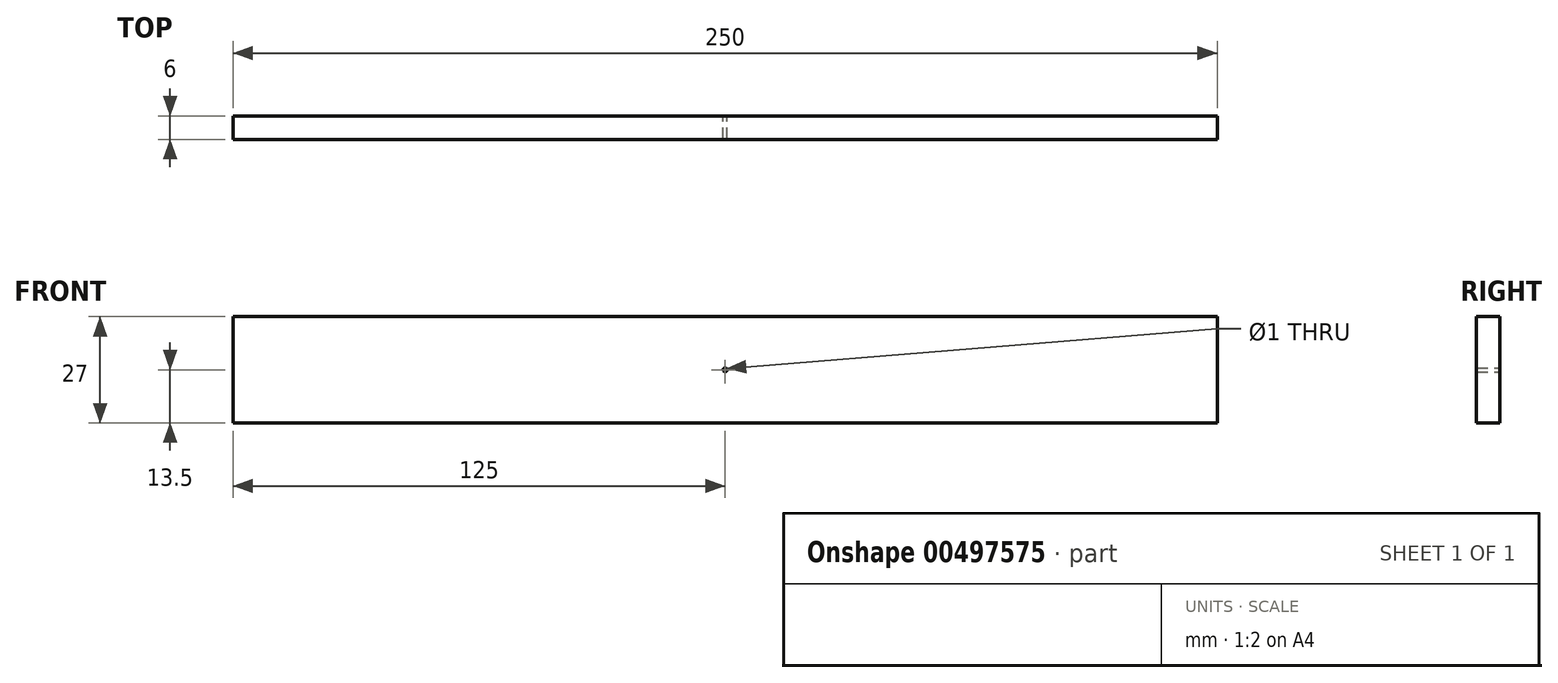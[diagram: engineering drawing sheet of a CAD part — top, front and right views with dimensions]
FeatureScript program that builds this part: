
annotation { "Feature Type Name" : "Feature", "Feature Type Description" : "" }
export const myFeature = defineFeature(function(context is Context, id is Id, definition is map)
    precondition{}
    {
        {
            var Q0;
            Q0=qCreatedBy(makeId("Front.planeOp"),FACE);
            var sketch = newSketch(context, id + "F0", { "sketchPlane" : qUnion([Q0])});
            skLineSegment(sketch, "E0.bottom", {"start": v(0, 0) * mm, "end": v(250, 0) * mm});
            skLineSegment(sketch, "E0.top", {"start": v(0, 27) * mm, "end": v(250, 27) * mm});
            skLineSegment(sketch, "E0.left", {"start": v(0, 0) * mm, "end": v(0, 27) * mm});
            skLineSegment(sketch, "E0.right", {"start": v(250, 0) * mm, "end": v(250, 27) * mm});
            skCircle(sketch, "E1", {"center": v(125, 13.5) * mm, "radius": 0.5 * mm});
            skPoint(sketch, "E1.centerSnap0", {"position": v(0, 13.5) * mm});
            skPoint(sketch, "E1.centerSnap1", {"position": v(125, 0) * mm});
            skSolve(sketch);
        }
        {
            var Q0;
            Q0 = qSketchRegion(id + "F0", true);
            extrude(context, id + "F1", {"entities" : qUnion([Q0]), "depth" : 6 * mm, "offsetDistance" : 25.4 * mm});
        }
    });
